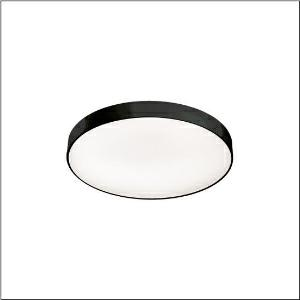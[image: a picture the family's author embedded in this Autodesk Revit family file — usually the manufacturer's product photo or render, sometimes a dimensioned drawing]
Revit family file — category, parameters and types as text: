
# Revit family: round_21_m_51mr36nd0421b
name_source: partatom
category: Lighting Fixtures
units: mm (PartAtom-declared; Revit-internal decimal feet)

## family parameters
Cut with Voids When Loaded = No
Host = Face
Light Source = No
Part Type = Normal
Room Calculation Point = No
Round Connector Dimension = Use Diameter
Shared = No

## types (1)
- Round 21 M (1 x LED, 7470 lm, 54.6 W, 4000K)
    Apparent Load = 55 VA
    CIE Flux Codes = 66 90 98 84 100
    Color Rendering = 80
    Color Temperature = 4000K
    Default Elevation = 1800 mm
    Description = Round 21 M, wall and ceiling luminaire, primary optical cover: micro prismatic cover, of PMMA, transparent, CAT 2 (L<= 3000cd/m²), light emission: direct/indirect distribution, primary light characteristic: symmetric, installation type: surface-mounted, suspended mounting, LED, rated luminous flux: 7.470lm, luminous efficacy: 137lm/W, light colour: 840, colour temperature: 4000K, with terminal, 5-pole, mains connection: 230V, AC, 50/60Hz, rated input power: 54.6W, housing, of aluminium, coated, black, diameter: 600mm, height: 62mm, protection rating (complete): IP40, insulation class (complete): insulation class I (protective earthing), certification: CE, impact resistance: IK04, permissible operating ambient temperature: -10..+35°C, packaging unit: 1 piece
    Height = 87 mm
    Lamp = 1 x LED
    Lamp Light Flux = 7470 lm
    Lamp Power = 54.6 W
    Lamp count = 1
    Length = 600 mm
    Luminous efficacy = 137 lm/W
    Manufacturer = Siteco
    ModVariant = No
    Model = 51MR36ND0421B
    Mounting Place = Ceiling
    Mounting Type = Surface mounted
    Number of Poles = 1
    OnlyDefault = Yes
    Power Factor = 1
    Product Name = Round 21 M
    Product group = wall and ceiling luminaire
    ProductGroupID = 303
    Protection Class = Protection class I
    Protection Degree = IP 40
    RLX_Detail_Level = 1
    RLX_Emergency_Light_Flux = 0 lm
    RLX_Emergency_Type = 0
    RLX_Emergency_Type_DB = No
    RlxData = <blob elided: 21917 chars, md5=3528e159>
    Socket = socket
    Standby Power = 0 W
    System Light Flux = 7470 lm
    System Power = 55 W
    Type Comments = Product without accessories
    Type Image = l_1258305.jpg
    URL = http://relux.com
    VarID = ---
    Voltage = 0 V
    Weight = 0.00 kg
    Width = 0 mm  [stored 0 ft]

note: [stored X ft] marks values corroborated as IEEE doubles in the binary element streams (Revit-internal decimal feet)

## geometry (parser evidence)
native form markers: Blend x4, Sweep x15
no freeform markers — native parametric forms only
